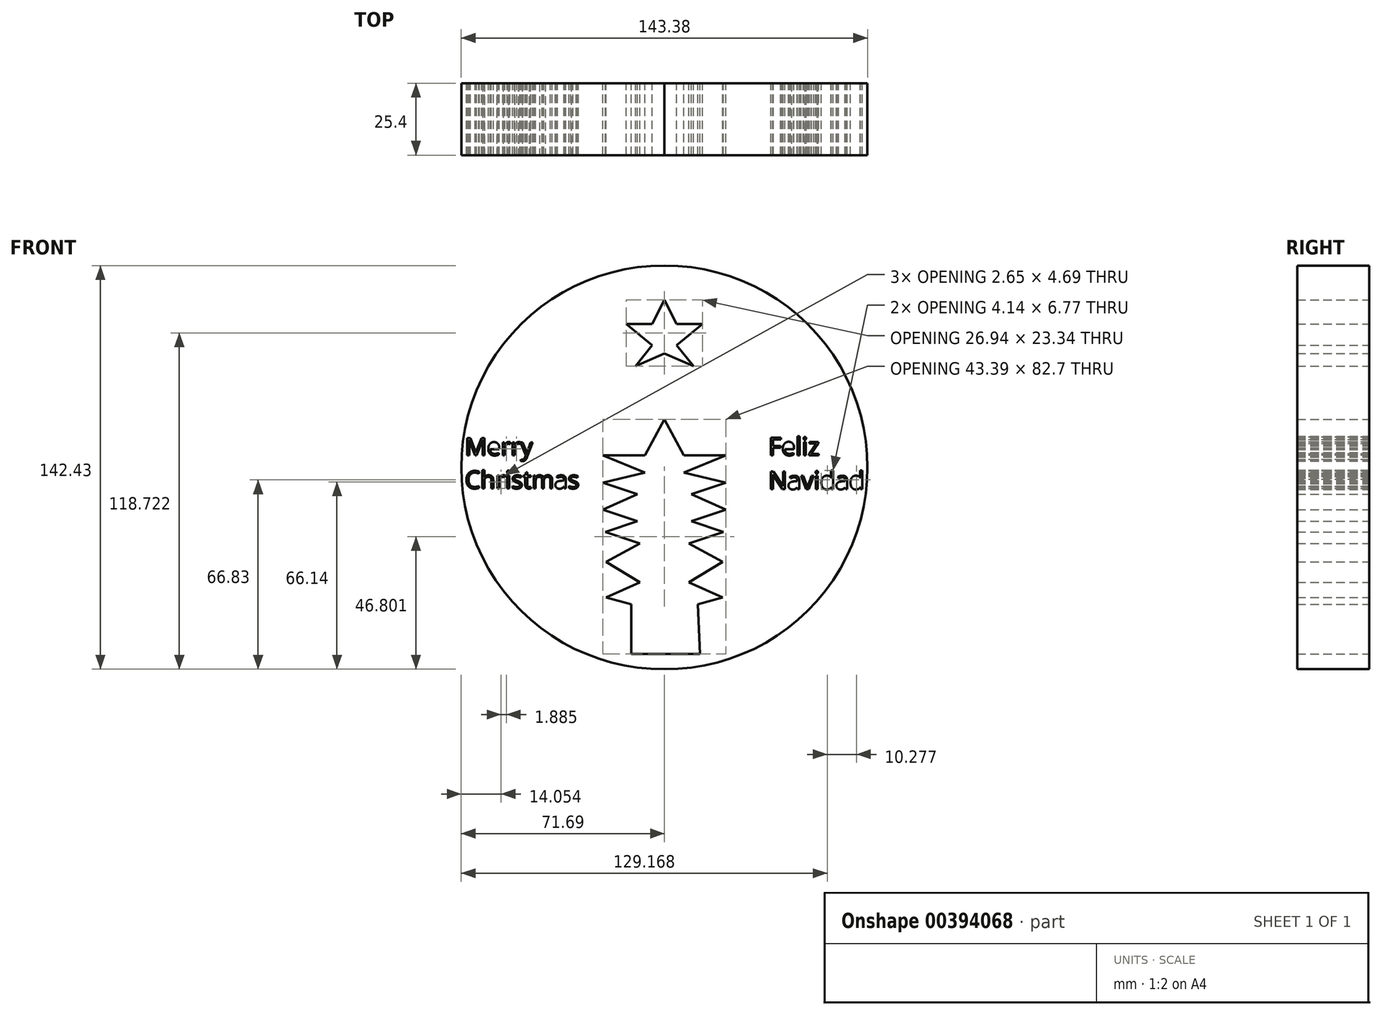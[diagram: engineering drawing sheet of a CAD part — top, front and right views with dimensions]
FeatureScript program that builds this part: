
annotation { "Feature Type Name" : "Feature", "Feature Type Description" : "" }
export const myFeature = defineFeature(function(context is Context, id is Id, definition is map)
    precondition{}
    {
        {
            var Q0;
            Q0=qCreatedBy(makeId("Front.planeOp"),FACE);
            var sketch = newSketch(context, id + "F0", { "sketchPlane" : qUnion([Q0])});
            skLineSegment(sketch, "E0", {"start": v(0, 12.66) * mm, "end": v(-6.9, 0) * mm});
            skLineSegment(sketch, "E1", {"start": v(0, 12.66) * mm, "end": v(6.9, 0) * mm});
            skLineSegment(sketch, "E2", {"start": v(-6.9, 0) * mm, "end": v(-21.7, 0) * mm});
            skLineSegment(sketch, "E3", {"start": v(-21.7, 0) * mm, "end": v(-6.9, -6.08) * mm});
            skLineSegment(sketch, "E4", {"start": v(-6.9, -6.08) * mm, "end": v(-21.7, -9.69) * mm});
            skLineSegment(sketch, "E5", {"start": v(-21.7, -9.69) * mm, "end": v(-9.54, -13.74) * mm});
            skLineSegment(sketch, "E6", {"start": v(-9.54, -13.74) * mm, "end": v(-21.7, -19.23) * mm});
            skLineSegment(sketch, "E7", {"start": v(-21.7, -19.23) * mm, "end": v(-9.54, -23.28) * mm});
            skLineSegment(sketch, "E8", {"start": v(-9.54, -23.28) * mm, "end": v(-20.83, -27.04) * mm});
            skLineSegment(sketch, "E9", {"start": v(-20.83, -27.04) * mm, "end": v(-8.68, -31.1) * mm});
            skLineSegment(sketch, "E10", {"start": v(-8.68, -31.1) * mm, "end": v(-20.53, -37.64) * mm});
            skLineSegment(sketch, "E11", {"start": v(-20.53, -37.64) * mm, "end": v(-8.68, -44.79) * mm});
            skLineSegment(sketch, "E12", {"start": v(-8.68, -44.79) * mm, "end": v(-20.53, -50.14) * mm});
            skLineSegment(sketch, "E13", {"start": v(-20.53, -50.14) * mm, "end": v(-11.75, -52.58) * mm});
            skLineSegment(sketch, "E14.MirrorCS", {"start": v(20.53, -50.14) * mm, "end": v(11.75, -52.58) * mm});
            skLineSegment(sketch, "E15.MirrorCS", {"start": v(8.68, -44.79) * mm, "end": v(20.53, -50.14) * mm});
            skLineSegment(sketch, "E16.MirrorCS", {"start": v(20.53, -37.64) * mm, "end": v(8.68, -44.79) * mm});
            skLineSegment(sketch, "E17.MirrorCS", {"start": v(8.68, -31.1) * mm, "end": v(20.53, -37.64) * mm});
            skLineSegment(sketch, "E18.MirrorCS", {"start": v(20.83, -27.04) * mm, "end": v(8.68, -31.1) * mm});
            skLineSegment(sketch, "E19.MirrorCS", {"start": v(9.54, -23.28) * mm, "end": v(20.83, -27.04) * mm});
            skLineSegment(sketch, "E20.MirrorCS", {"start": v(21.7, -19.23) * mm, "end": v(9.54, -23.28) * mm});
            skLineSegment(sketch, "E21.MirrorCS", {"start": v(9.54, -13.74) * mm, "end": v(21.7, -19.23) * mm});
            skLineSegment(sketch, "E22.MirrorCS", {"start": v(21.7, -9.69) * mm, "end": v(9.54, -13.74) * mm});
            skLineSegment(sketch, "E23.MirrorCS", {"start": v(6.9, -6.08) * mm, "end": v(21.7, -9.69) * mm});
            skLineSegment(sketch, "E24.MirrorCS", {"start": v(6.9, 0) * mm, "end": v(21.7, 0) * mm});
            skLineSegment(sketch, "E25.MirrorCS", {"start": v(21.7, 0) * mm, "end": v(6.9, -6.08) * mm});
            skLineSegment(sketch, "E26", {"start": v(-11.75, -52.58) * mm, "end": v(-11.75, -70.04) * mm});
            skLineSegment(sketch, "E27", {"start": v(12.6, -70.04) * mm, "end": v(11.75, -52.58) * mm});
            skLineSegment(sketch, "E28", {"start": v(0, 54.9) * mm, "end": v(-4.3, 46.3) * mm});
            skLineSegment(sketch, "E29", {"start": v(-4.3, 46.3) * mm, "end": v(-13.47, 46.3) * mm});
            skLineSegment(sketch, "E30", {"start": v(-13.47, 46.3) * mm, "end": v(-4.3, 38.85) * mm});
            skLineSegment(sketch, "E31", {"start": v(-4.3, 38.85) * mm, "end": v(-10.22, 31.56) * mm});
            skLineSegment(sketch, "E32", {"start": v(-10.22, 31.56) * mm, "end": v(0, 35.99) * mm});
            skLineSegment(sketch, "E33.MirrorCS", {"start": v(10.22, 31.56) * mm, "end": v(0, 35.99) * mm});
            skLineSegment(sketch, "E34.MirrorCS", {"start": v(4.3, 38.85) * mm, "end": v(10.22, 31.56) * mm});
            skLineSegment(sketch, "E35.MirrorCS", {"start": v(13.47, 46.3) * mm, "end": v(4.3, 38.85) * mm});
            skLineSegment(sketch, "E36.MirrorCS", {"start": v(0, 54.9) * mm, "end": v(4.3, 46.3) * mm});
            skLineSegment(sketch, "E37.MirrorCS", {"start": v(4.3, 46.3) * mm, "end": v(13.47, 46.3) * mm});
            skLineSegment(sketch, "E38", {"start": v(-11.75, -70.04) * mm, "end": v(12.6, -70.04) * mm});
            skArc(sketch, "E39", {"start": v(0, 66.94) * mm, "mid": v(-71.69, -4.27) * mm, "end": v(0, -75.48) * mm});
            skArc(sketch, "E40.MirrorCS", {"start": v(0, 66.94) * mm, "mid": v(71.69, -4.27) * mm, "end": v(0, -75.48) * mm});
            skText(sketch, "E41", { "text": "Merry\nChristmas", "fontName": "OpenSans-Regular.ttf"});
            skText(sketch, "E42", { "text": "Feliz \nNavidad", "fontName": "OpenSans-Regular.ttf"});
            skPoint(sketch, "E42.firstSnap0", {"position": v(3.45, 6.33) * mm});
            const initialGuessF0  = {"E41": [-0.0704, 0, 1, 0, 0.00619], "E42": [0.03677, 0, 1, 0, 0.00633]};
            skSetInitialGuess(sketch, initialGuessF0);
            skSolve(sketch);
        }
        {
            var Q0;
            Q0=makeQuery(id+"F0.imprint","IMPRINT",FACE,{"disambiguationData":[TD([[makeQuery(id+"F0.imprint","IMPRINT",EDGE,{"derivedFrom":sQuery(id+"F0.wireOp",EDGE,"E0")}),-1.0]])]});
            extrude(context, id + "F1", {"entities" : qUnion([Q0]), "depth" : 25.4 * mm});
        }
    });
